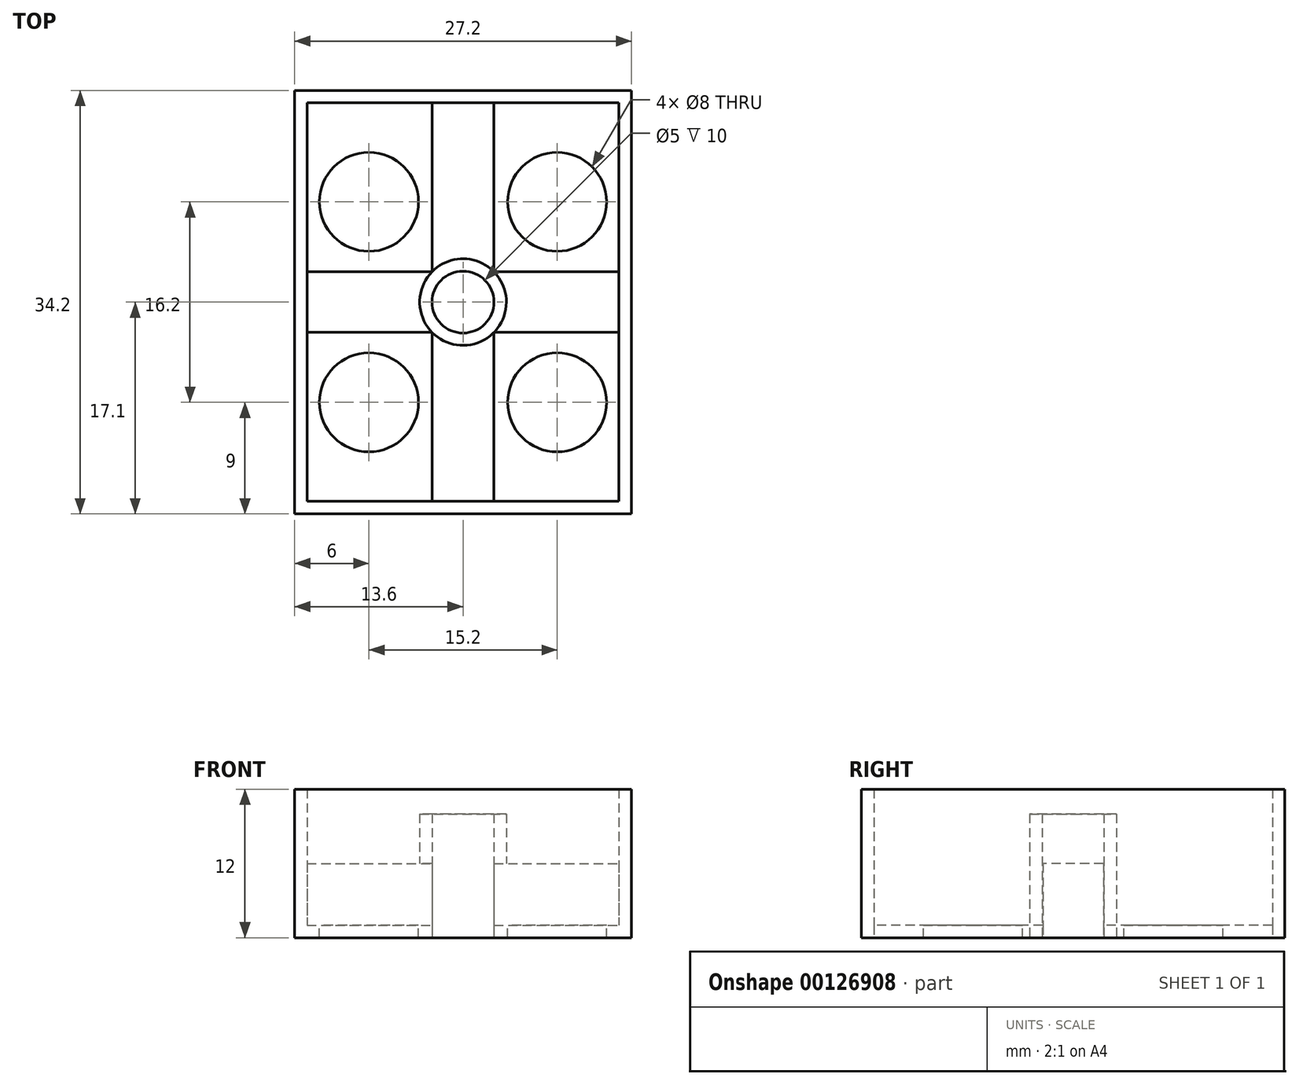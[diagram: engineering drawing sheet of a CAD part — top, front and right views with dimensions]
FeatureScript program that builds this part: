
annotation { "Feature Type Name" : "Feature", "Feature Type Description" : "" }
export const myFeature = defineFeature(function(context is Context, id is Id, definition is map)
    precondition{}
    {
        {
            var Q0;
            Q0=qCreatedBy(makeId("Top.planeOp"),FACE);
            var sketch = newSketch(context, id + "F0", { "sketchPlane" : qUnion([Q0])});
            skLineSegment(sketch, "E0.bottom", {"start": v(12.6, 16.1) * mm, "end": v(-12.6, 16.1) * mm});
            skLineSegment(sketch, "E0.top", {"start": v(12.6, -16.1) * mm, "end": v(-12.6, -16.1) * mm});
            skLineSegment(sketch, "E0.left", {"start": v(12.6, 16.1) * mm, "end": v(12.6, -16.1) * mm});
            skLineSegment(sketch, "E0.right", {"start": v(-12.6, 16.1) * mm, "end": v(-12.6, -16.1) * mm});
            skPoint(sketch, "E0.middle", {"position": v(0, 0) * mm});
            skLineSegment(sketch, "E1.bottom", {"start": v(13.6, 17.1) * mm, "end": v(-13.6, 17.1) * mm});
            skLineSegment(sketch, "E1.top", {"start": v(13.6, -17.1) * mm, "end": v(-13.6, -17.1) * mm});
            skLineSegment(sketch, "E1.left", {"start": v(13.6, 17.1) * mm, "end": v(13.6, -17.1) * mm});
            skLineSegment(sketch, "E1.right", {"start": v(-13.6, 17.1) * mm, "end": v(-13.6, -17.1) * mm});
            skSolve(sketch);
        }
        {
            var Q0;
            Q0=makeQuery(id+"F0.imprint","IMPRINT",FACE,{"disambiguationData":[TD([[makeQuery(id+"F0.imprint","IMPRINT",EDGE,{"derivedFrom":sQuery(id+"F0.wireOp",EDGE,"E0.bottom")}),-1.0]])]});
            extrude(context, id + "F1", {"entities" : qUnion([Q0]), "depth" : 12 * mm});
        }
        {
            var Q0;
            Q0=qCreatedBy(makeId("Top.planeOp"),FACE);
            var sketch = newSketch(context, id + "F2", { "sketchPlane" : qUnion([Q0])});
            skPoint(sketch, "E2.0", {"position": v(-12.6, 16.1) * mm});
            skPoint(sketch, "E3.0", {"position": v(12.6, -16.1) * mm});
            skPoint(sketch, "E4.0", {"position": v(-12.6, -16.1) * mm});
            skPoint(sketch, "E5.0", {"position": v(12.6, 16.1) * mm});
            skLineSegment(sketch, "E6.bottom", {"start": v(-12.6, 16.1) * mm, "end": v(-2.5, 16.1) * mm});
            skLineSegment(sketch, "E6.top", {"start": v(-12.6, -16.1) * mm, "end": v(-2.5, -16.1) * mm});
            skLineSegment(sketch, "E6.left", {"start": v(-12.6, 16.1) * mm, "end": v(-12.6, -16.1) * mm});
            skLineSegment(sketch, "E6.right", {"start": v(-2.5, 16.1) * mm, "end": v(-2.5, -16.1) * mm});
            skLineSegment(sketch, "E7.bottom", {"start": v(12.6, 16.1) * mm, "end": v(2.5, 16.1) * mm});
            skLineSegment(sketch, "E7.top", {"start": v(12.6, -16.1) * mm, "end": v(2.5, -16.1) * mm});
            skLineSegment(sketch, "E7.left", {"start": v(12.6, 16.1) * mm, "end": v(12.6, -16.1) * mm});
            skLineSegment(sketch, "E7.right", {"start": v(2.5, 16.1) * mm, "end": v(2.5, -16.1) * mm});
            skSolve(sketch);
        }
        {
            var Q0;
            Q0=makeQuery(id+"F2.imprint","IMPRINT",FACE,{"disambiguationData":[TD([[makeQuery(id+"F2.imprint","IMPRINT",EDGE,{"derivedFrom":sQuery(id+"F2.wireOp",EDGE,"E6.bottom")}),-1.0]])]});
            var Q1;
            Q1=makeQuery(id+"F2.imprint","IMPRINT",FACE,{"disambiguationData":[TD([[makeQuery(id+"F2.imprint","IMPRINT",EDGE,{"derivedFrom":sQuery(id+"F2.wireOp",EDGE,"E7.bottom")}),1.0]])]});
            extrude(context, id + "F3", {"entities" : qUnion([Q0, Q1]), "operationType" : NewBodyOperationType.ADD, "depth" : 1 * mm});
        }
        {
            var Q0;
            Q0=qCreatedBy(makeId("Top.planeOp"),FACE);
            var sketch = newSketch(context, id + "F4", { "sketchPlane" : qUnion([Q0])});
            skCircle(sketch, "E8", {"center": v(0, 0) * mm, "radius": 2.5 * mm});
            skCircle(sketch, "E9", {"center": v(0, 0) * mm, "radius": 3.5 * mm});
            skSolve(sketch);
        }
        {
            var Q0;
            Q0=makeQuery(id+"F4.imprint","IMPRINT",FACE,{"disambiguationData":[TD([[makeQuery(id+"F4.imprint","IMPRINT",EDGE,{"derivedFrom":sQuery(id+"F4.wireOp",EDGE,"E8")}),-1.0]])]});
            extrude(context, id + "F5", {"entities" : qUnion([Q0]), "operationType" : NewBodyOperationType.ADD, "depth" : 10 * mm});
        }
        {
            var Q0;
            Q0=makeQuery(id+"F3.opExtrude","CAP_FACE",FACE,{"disambiguationData":[OSD([sQuery(id+"F2.wireOp",EDGE,"E6.bottom"),sQuery(id+"F2.wireOp",EDGE,"E6.top"),sQuery(id+"F2.wireOp",EDGE,"E6.left"),sQuery(id+"F2.wireOp",EDGE,"E6.right")])],"isStart":false});
            var sketch = newSketch(context, id + "F6", { "sketchPlane" : qUnion([Q0])});
            skLineSegment(sketch, "E10.bottom", {"start": v(-7.6, 8.1) * mm, "end": v(7.6, 8.1) * mm});
            skLineSegment(sketch, "E10.top", {"start": v(-7.6, -8.1) * mm, "end": v(7.6, -8.1) * mm});
            skLineSegment(sketch, "E10.left", {"start": v(-7.6, 8.1) * mm, "end": v(-7.6, -8.1) * mm});
            skLineSegment(sketch, "E10.right", {"start": v(7.6, 8.1) * mm, "end": v(7.6, -8.1) * mm});
            skCircle(sketch, "E11", {"center": v(-7.6, 8.1) * mm, "radius": 4 * mm});
            skCircle(sketch, "E12", {"center": v(7.6, 8.1) * mm, "radius": 4 * mm});
            skCircle(sketch, "E13", {"center": v(7.6, -8.1) * mm, "radius": 4 * mm});
            skCircle(sketch, "E14", {"center": v(-7.6, -8.1) * mm, "radius": 4 * mm});
            skSolve(sketch);
        }
        {
            var Q0;
            {var subQ0=sQuery(id+"F6.wireOp",EDGE,"E10.left");var subQ1=sQuery(id+"F6.wireOp",EDGE,"E10.bottom");var subQ2=makeQuery(id+"F6.imprint","INTERSECT",VERTEX,{"derivedFrom":[subQ1,subQ0]});Q0=makeQuery(id+"F6.imprint","IMPRINT",FACE,{"disambiguationData":[TD([[makeQuery(id+"F6.imprint","IMPRINT",EDGE,{"disambiguationData":[TD([[subQ2,-1.0]])],"derivedFrom":subQ1}),1.0]])]});}
            var Q1;
            {var subQ0=sQuery(id+"F6.wireOp",EDGE,"E10.right");var subQ1=sQuery(id+"F6.wireOp",EDGE,"E10.bottom");var subQ2=makeQuery(id+"F6.imprint","INTERSECT",VERTEX,{"derivedFrom":[subQ1,subQ0]});Q1=makeQuery(id+"F6.imprint","IMPRINT",FACE,{"disambiguationData":[TD([[makeQuery(id+"F6.imprint","IMPRINT",EDGE,{"disambiguationData":[TD([[subQ2,1.0]])],"derivedFrom":subQ1}),1.0]])]});}
            var Q2;
            {var subQ0=sQuery(id+"F6.wireOp",EDGE,"E10.right");var subQ1=sQuery(id+"F6.wireOp",EDGE,"E10.bottom");var subQ2=makeQuery(id+"F6.imprint","INTERSECT",VERTEX,{"derivedFrom":[subQ1,subQ0]});Q2=makeQuery(id+"F6.imprint","IMPRINT",FACE,{"disambiguationData":[TD([[makeQuery(id+"F6.imprint","IMPRINT",EDGE,{"disambiguationData":[TD([[subQ2,1.0]])],"derivedFrom":subQ1}),-1.0]])]});}
            var Q3;
            {var subQ0=sQuery(id+"F6.wireOp",EDGE,"E10.left");var subQ1=sQuery(id+"F6.wireOp",EDGE,"E10.bottom");var subQ2=makeQuery(id+"F6.imprint","INTERSECT",VERTEX,{"derivedFrom":[subQ1,subQ0]});Q3=makeQuery(id+"F6.imprint","IMPRINT",FACE,{"disambiguationData":[TD([[makeQuery(id+"F6.imprint","IMPRINT",EDGE,{"disambiguationData":[TD([[subQ2,-1.0]])],"derivedFrom":subQ1}),-1.0]])]});}
            var Q4;
            {var subQ0=sQuery(id+"F6.wireOp",EDGE,"E10.left");var subQ1=sQuery(id+"F6.wireOp",EDGE,"E10.top");var subQ2=makeQuery(id+"F6.imprint","INTERSECT",VERTEX,{"derivedFrom":[subQ1,subQ0]});Q4=makeQuery(id+"F6.imprint","IMPRINT",FACE,{"disambiguationData":[TD([[makeQuery(id+"F6.imprint","IMPRINT",EDGE,{"disambiguationData":[TD([[subQ2,-1.0]])],"derivedFrom":subQ1}),-1.0]])]});}
            var Q5;
            {var subQ0=sQuery(id+"F6.wireOp",EDGE,"E10.left");var subQ1=sQuery(id+"F6.wireOp",EDGE,"E10.top");var subQ2=makeQuery(id+"F6.imprint","INTERSECT",VERTEX,{"derivedFrom":[subQ1,subQ0]});Q5=makeQuery(id+"F6.imprint","IMPRINT",FACE,{"disambiguationData":[TD([[makeQuery(id+"F6.imprint","IMPRINT",EDGE,{"disambiguationData":[TD([[subQ2,-1.0]])],"derivedFrom":subQ1}),1.0]])]});}
            var Q6;
            {var subQ0=sQuery(id+"F6.wireOp",EDGE,"E10.right");var subQ1=sQuery(id+"F6.wireOp",EDGE,"E10.top");var subQ2=makeQuery(id+"F6.imprint","INTERSECT",VERTEX,{"derivedFrom":[subQ1,subQ0]});Q6=makeQuery(id+"F6.imprint","IMPRINT",FACE,{"disambiguationData":[TD([[makeQuery(id+"F6.imprint","IMPRINT",EDGE,{"disambiguationData":[TD([[subQ2,1.0]])],"derivedFrom":subQ1}),-1.0]])]});}
            var Q7;
            {var subQ0=sQuery(id+"F6.wireOp",EDGE,"E10.right");var subQ1=sQuery(id+"F6.wireOp",EDGE,"E10.top");var subQ2=makeQuery(id+"F6.imprint","INTERSECT",VERTEX,{"derivedFrom":[subQ1,subQ0]});Q7=makeQuery(id+"F6.imprint","IMPRINT",FACE,{"disambiguationData":[TD([[makeQuery(id+"F6.imprint","IMPRINT",EDGE,{"disambiguationData":[TD([[subQ2,1.0]])],"derivedFrom":subQ1}),1.0]])]});}
            extrude(context, id + "F7", {"entities" : qUnion([Q0, Q1, Q2, Q3, Q4, Q5, Q6, Q7]), "operationType" : NewBodyOperationType.REMOVE, "oppositeDirection" : true, "depth" : 25.4 * mm});
        }
        {
            var Q0;
            Q0=makeQuery(id+"F3.opExtrude","CAP_FACE",FACE,{"disambiguationData":[OSD([sQuery(id+"F2.wireOp",EDGE,"E6.bottom"),sQuery(id+"F2.wireOp",EDGE,"E6.top"),sQuery(id+"F2.wireOp",EDGE,"E6.left"),sQuery(id+"F2.wireOp",EDGE,"E6.right")])],"isStart":false});
            var sketch = newSketch(context, id + "F8", { "sketchPlane" : qUnion([Q0])});
            skLineSegment(sketch, "E15.bottom", {"start": v(-12.6, -2.45) * mm, "end": v(-2.5, -2.45) * mm});
            skLineSegment(sketch, "E15.top", {"start": v(-12.6, 2.45) * mm, "end": v(-2.5, 2.45) * mm});
            skLineSegment(sketch, "E15.left", {"start": v(-12.6, -2.45) * mm, "end": v(-12.6, 2.45) * mm});
            skLineSegment(sketch, "E15.right", {"start": v(-2.5, -2.45) * mm, "end": v(-2.5, 2.45) * mm});
            skLineSegment(sketch, "E16.bottom", {"start": v(2.5, 2.45) * mm, "end": v(12.6, 2.45) * mm});
            skLineSegment(sketch, "E16.top", {"start": v(2.5, -2.45) * mm, "end": v(12.6, -2.45) * mm});
            skLineSegment(sketch, "E16.left", {"start": v(2.5, 2.45) * mm, "end": v(2.5, -2.45) * mm});
            skLineSegment(sketch, "E16.right", {"start": v(12.6, 2.45) * mm, "end": v(12.6, -2.45) * mm});
            skSolve(sketch);
        }
        {
            var Q0;
            Q0=makeQuery(id+"F8.imprint","IMPRINT",FACE,{"disambiguationData":[TD([[makeQuery(id+"F8.imprint","IMPRINT",EDGE,{"derivedFrom":sQuery(id+"F8.wireOp",EDGE,"E15.bottom")}),1.0]])]});
            var Q1;
            Q1=makeQuery(id+"F8.imprint","IMPRINT",FACE,{"disambiguationData":[TD([[makeQuery(id+"F8.imprint","IMPRINT",EDGE,{"derivedFrom":sQuery(id+"F8.wireOp",EDGE,"E16.bottom")}),-1.0]])]});
            extrude(context, id + "F9", {"entities" : qUnion([Q0, Q1]), "operationType" : NewBodyOperationType.ADD, "depth" : 5 * mm});
        }
    });
